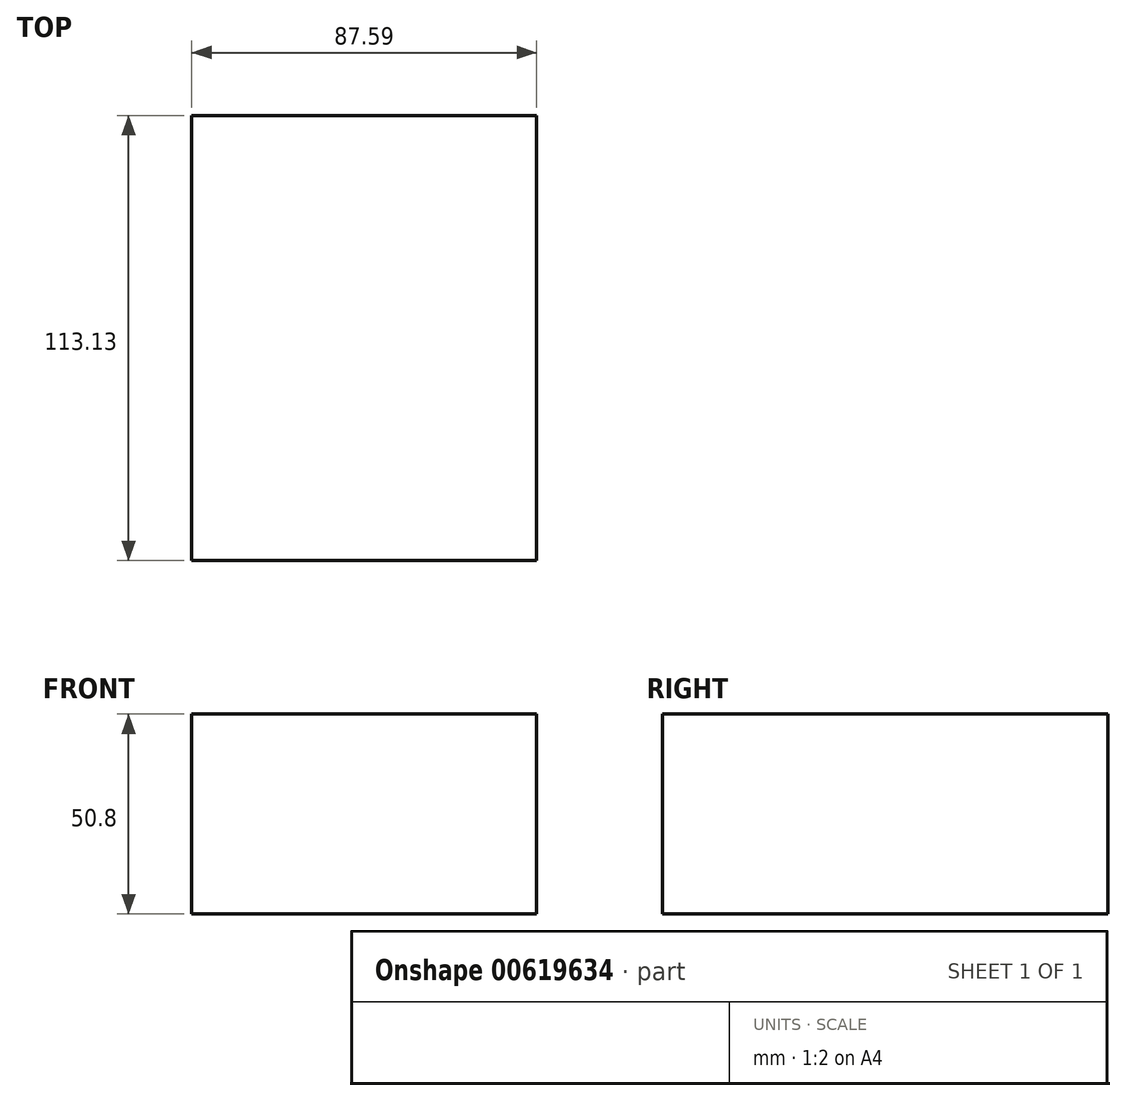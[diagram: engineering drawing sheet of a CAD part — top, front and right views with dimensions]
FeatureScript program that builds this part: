
annotation { "Feature Type Name" : "Feature", "Feature Type Description" : "" }
export const myFeature = defineFeature(function(context is Context, id is Id, definition is map)
    precondition{}
    {
        {
            var Q0;
            Q0=qCreatedBy(makeId("Top.planeOp"),FACE);
            var sketch = newSketch(context, id + "F0", { "sketchPlane" : qUnion([Q0])});
            skLineSegment(sketch, "E0.bottom", {"start": v(-58.86, -60.84) * mm, "end": v(28.73, -60.84) * mm});
            skLineSegment(sketch, "E0.top", {"start": v(-58.86, 52.29) * mm, "end": v(28.73, 52.29) * mm});
            skLineSegment(sketch, "E0.left", {"start": v(-58.86, -60.84) * mm, "end": v(-58.86, 52.29) * mm});
            skLineSegment(sketch, "E0.right", {"start": v(28.73, -60.84) * mm, "end": v(28.73, 52.29) * mm});
            skSolve(sketch);
        }
        {
            var Q0;
            Q0 = qSketchRegion(id + "F0", true);
            extrude(context, id + "F1", {"entities" : qUnion([Q0]), "depth" : 50.8 * mm, "offsetDistance" : 25.4 * mm});
        }
    });
